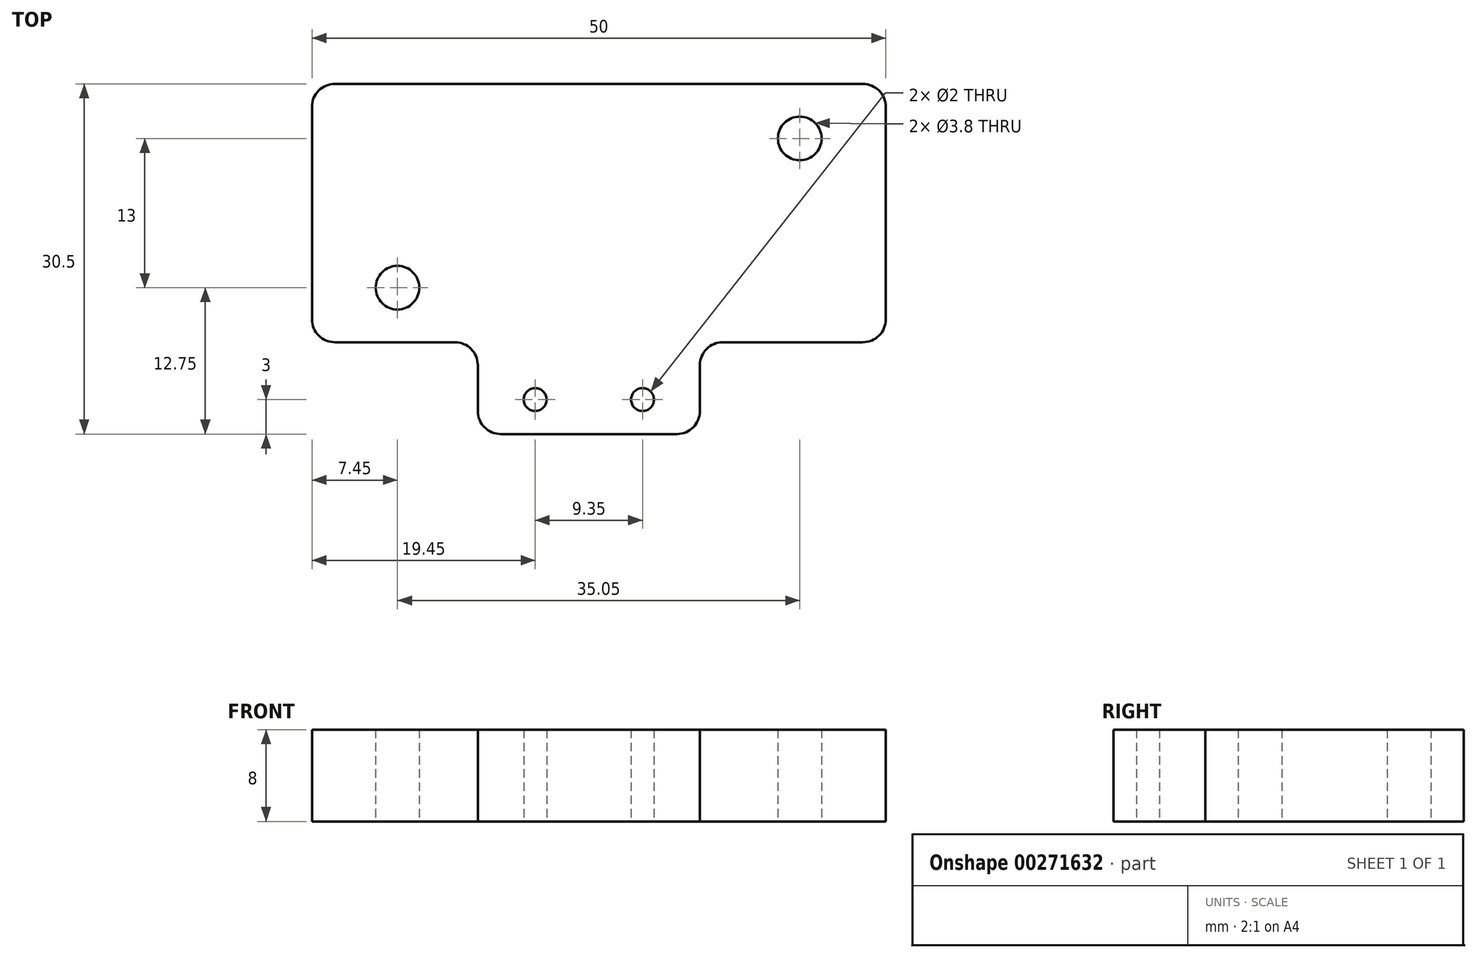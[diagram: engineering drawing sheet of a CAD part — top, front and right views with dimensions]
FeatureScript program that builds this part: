
annotation { "Feature Type Name" : "Feature", "Feature Type Description" : "" }
export const myFeature = defineFeature(function(context is Context, id is Id, definition is map)
    precondition{}
    {
        {
            var Q0;
            Q0=qCreatedBy(makeId("Top.planeOp"),FACE);
            var sketch = newSketch(context, id + "F0", { "sketchPlane" : qUnion([Q0])});
            skCircle(sketch, "E0", {"center": v(42.5, 17.75) * mm, "radius": 1.9 * mm});
            skCircle(sketch, "E1", {"center": v(7.45, 4.75) * mm, "radius": 1.9 * mm});
            skLineSegment(sketch, "E2.bottom", {"start": v(0, 22.5) * mm, "end": v(50, 22.5) * mm});
            skLineSegment(sketch, "E2.top", {"start": v(0, 0) * mm, "end": v(50, 0) * mm});
            skLineSegment(sketch, "E2.left", {"start": v(0, 22.5) * mm, "end": v(0, 0) * mm});
            skLineSegment(sketch, "E2.right", {"start": v(50, 22.5) * mm, "end": v(50, 0) * mm});
            skCircle(sketch, "E3", {"center": v(19.45, -5) * mm, "radius": 1 * mm});
            skCircle(sketch, "E4", {"center": v(28.8, -5) * mm, "radius": 1 * mm});
            skLineSegment(sketch, "E5.bottom", {"start": v(14.45, 0) * mm, "end": v(33.8, 0) * mm});
            skLineSegment(sketch, "E5.top", {"start": v(14.45, -8) * mm, "end": v(33.8, -8) * mm});
            skLineSegment(sketch, "E5.left", {"start": v(14.45, 0) * mm, "end": v(14.45, -8) * mm});
            skLineSegment(sketch, "E5.right", {"start": v(33.8, 0) * mm, "end": v(33.8, -8) * mm});
            skSolve(sketch);
        }
        {
            var Q0;
            Q0=makeQuery(id+"F0.imprint","IMPRINT",FACE,{"disambiguationData":[TD([[makeQuery(id+"F0.imprint","IMPRINT",EDGE,{"derivedFrom":sQuery(id+"F0.wireOp",EDGE,"E0")}),-1.0]])]});
            var Q1;
            Q1=makeQuery(id+"F0.imprint","IMPRINT",FACE,{"disambiguationData":[TD([[makeQuery(id+"F0.imprint","IMPRINT",EDGE,{"derivedFrom":sQuery(id+"F0.wireOp",EDGE,"E3")}),-1.0]])]});
            extrude(context, id + "F1", {"entities" : qUnion([Q0, Q1]), "depth" : 8 * mm});
        }
        {
            var Q0;
            Q0=makeQuery(id+"F1.opExtrude","SWEPT_EDGE",EDGE,{"disambiguationData":[OSD([sQuery(id+"F0.wireOp",EDGE,"E2.top"),sQuery(id+"F0.wireOp",EDGE,"E5.bottom"),sQuery(id+"F0.wireOp",EDGE,"E5.left")])]});
            var Q1;
            Q1=makeQuery(id+"F1.opExtrude","SWEPT_EDGE",EDGE,{"disambiguationData":[OSD([sQuery(id+"F0.wireOp",EDGE,"E5.top"),sQuery(id+"F0.wireOp",EDGE,"E5.left")])]});
            var Q2;
            Q2=makeQuery(id+"F1.opExtrude","SWEPT_EDGE",EDGE,{"disambiguationData":[OSD([sQuery(id+"F0.wireOp",EDGE,"E5.top"),sQuery(id+"F0.wireOp",EDGE,"E5.right")])]});
            var Q3;
            Q3=makeQuery(id+"F1.opExtrude","SWEPT_EDGE",EDGE,{"disambiguationData":[OSD([sQuery(id+"F0.wireOp",EDGE,"E2.top"),sQuery(id+"F0.wireOp",EDGE,"E5.bottom"),sQuery(id+"F0.wireOp",EDGE,"E5.right")])]});
            var Q4;
            Q4=makeQuery(id+"F1.opExtrude","SWEPT_EDGE",EDGE,{"disambiguationData":[OSD([sQuery(id+"F0.wireOp",EDGE,"E2.top"),sQuery(id+"F0.wireOp",EDGE,"E2.right")])]});
            var Q5;
            Q5=makeQuery(id+"F1.opExtrude","SWEPT_EDGE",EDGE,{"disambiguationData":[OSD([sQuery(id+"F0.wireOp",EDGE,"E2.bottom"),sQuery(id+"F0.wireOp",EDGE,"E2.right")])]});
            var Q6;
            Q6=makeQuery(id+"F1.opExtrude","SWEPT_EDGE",EDGE,{"disambiguationData":[OSD([sQuery(id+"F0.wireOp",EDGE,"E2.top"),sQuery(id+"F0.wireOp",EDGE,"E2.left")])]});
            var Q7;
            Q7=makeQuery(id+"F1.opExtrude","SWEPT_EDGE",EDGE,{"disambiguationData":[OSD([sQuery(id+"F0.wireOp",EDGE,"E2.bottom"),sQuery(id+"F0.wireOp",EDGE,"E2.left")])]});
            fillet(context, id + "F2", {"entities" : qUnion([Q0, Q1, Q2, Q3, Q4, Q5, Q6, Q7]), "radius" : 2 * mm, "tangentPropagation" : true, "allowEdgeOverflow" : false});
        }
    });
